# Revit family: PARLÉ TCM-X - Ceiling Microphone_rev2
name_source: partatom
category: Communication Devices
units: mm (PartAtom-declared; Revit-internal decimal feet)

## family parameters
Cut with Voids When Loaded = No
Host = Face
Maintain Annotation Orientation = No
Part Type = Normal
Room Calculation Point = Yes
Round Connector Dimension = Use Diameter
Shared = Yes

## types (4) — shared parameters
Default Elevation = 4'-0"
Manufacturer = Biamp Systems
Manufacturer URL = https://www.biamp.com
Room Acoustics Examples URL = https://support.biamp.com

## per-type parameters (varying)
| type | Description | Drywall Kit Finish | Mic Finish | Model |
| PARLÉ™ TCM-X - Black | Parle Beamsteering Microphone Assembly (refer to component families for data and cost) | TCM-X-DK-Drywall Mounting Kit : TCM-X-DK - Black | PARLÉ TCM-X - Ceiling Microphone Base : PARLÉ™ TCM-X - Black | Parlé TCM-X Assembly |
| PARLÉ™ TCM-X - White | Parle Beamsteering Microphone Assembly (refer to component families for data and cost) | TCM-X-DK-Drywall Mounting Kit : TCM-X-DK - White | PARLÉ TCM-X - Ceiling Microphone Base : PARLÉ™ TCM-X - White | Parlé TCM-X Assembly |
| PARLÉ™ TCM-XEX - White | Parle Beamsteering Microphone Assembly - Expansion Mic. Must be used with TCM-X mic system. Cost for expamsion mic only. (refer to component families for data) | TCM-X-DK-Drywall Mounting Kit : TCM-X-DK - White | PARLÉ TCM-X - Ceiling Microphone Base : PARLÉ™ TCM-XEX - White | Parlé TCM-XEX Assembly |
| PARLÉ™ TCM-XEX - Black | Parle Beamsteering Microphone Assembly - Expansion Mic. Must be used with TCM-X mic system. Cost for expamsion mic only. (refer to component families for data) | TCM-X-DK-Drywall Mounting Kit : TCM-X-DK - Black | PARLÉ TCM-X - Ceiling Microphone Base : PARLÉ™ TCM-XEX - Black | Parlé TCM-XEX Assembly |

## geometry (parser evidence)
native form markers: Sweep x5
no freeform markers — native parametric forms only
